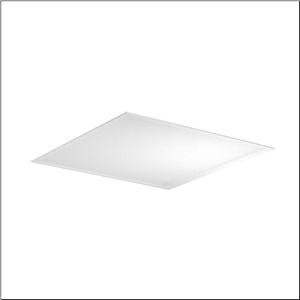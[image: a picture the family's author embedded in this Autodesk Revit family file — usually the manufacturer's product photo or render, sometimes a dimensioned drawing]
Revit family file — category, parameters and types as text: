
# Revit family: apollon_r__31_square_51mp12n72442_260a
name_source: partatom
category: Lighting Fixtures
units: mm (PartAtom-declared; Revit-internal decimal feet)

## family parameters
Cut with Voids When Loaded = No
Host = Face
Light Source = No
Part Type = Normal
Room Calculation Point = No
Round Connector Dimension = Use Diameter
Shared = No

## types (1)
- Apollon® 31 square (1 x LED, 4000 lm, 27.5 W, 4000K)
    Apparent Load = 28 VA
    CIE Flux Codes = 46 78 95 100 100
    Color Rendering = 80
    Color Temperature = 4000K
    Default Elevation = 1800 mm
    Description = Apollon® 31 square, office luminaire, primary optical cover: micro prismatic cover, of PMMA, CAT 2 (L<= 3000cd/m²), light emission: direct distribution, primary light characteristic: symmetric, installation type: lay-in mounting, LED, rated luminous flux: 4.000lm, luminous efficacy: 145lm/W, light colour: 840, colour temperature: 4000K, with terminal, 3-pole, mains connection: 220..240V, AC, 50/60Hz, rated input power: 28W, housing, of aluminium, traffic white (RAL 9016), module: M600, length: 595mm, width: 595mm, height: 32mm, housing upper side, of sheet steel, galvanised, protection rating (complete): IP20, protection rating (on room side): IP40, insulation class (complete): insulation class II (safety insulation), certification: CE, ENEC, impact resistance: IK03, permissible operating ambient temperature: -20..+40°C, permissible storage temperature: -20..+60°C, packaging unit: 1 piece
    Height = 0 mm  [stored 0 ft]
    Lamp = 1 x LED
    Lamp Light Flux = 4000 lm
    Lamp Power = 27.5 W
    Lamp count = 1
    Length = 595 mm
    Luminous efficacy = 145 lm/W
    Manufacturer = Siteco
    ModVariant = No
    Model = 51MP12N72442
    Mounting Place = Ceiling
    Mounting Type = Recessed
    Number of Poles = 1
    OnlyDefault = Yes
    Power Factor = 1
    Product Name = Apollon® 31 square
    Product group = office luminaire | ceiling recessed
    ProductGroupID = 401
    Protection Class = Protection class II
    Protection Degree = IP 20
    RLX_Detail_Level = 1
    RLX_Emergency_Light_Flux = 0 lm
    RLX_Emergency_Type = 0
    RLX_Emergency_Type_DB = No
    RlxData = <blob elided: 12317 chars, md5=fd6e380b>
    Socket = socket
    Standby Power = 0 W
    System Light Flux = 4000 lm
    System Power = 28 W
    Type Comments = Product without accessories
    Type Image = l_1291035.jpg
    URL = http://relux.com
    VarID = ---
    Voltage = 0 V
    Weight = 0.00 kg
    Width = 595 mm

note: [stored X ft] marks values corroborated as IEEE doubles in the binary element streams (Revit-internal decimal feet)

## geometry (parser evidence)
native form markers: Sweep x9
no freeform markers — native parametric forms only
